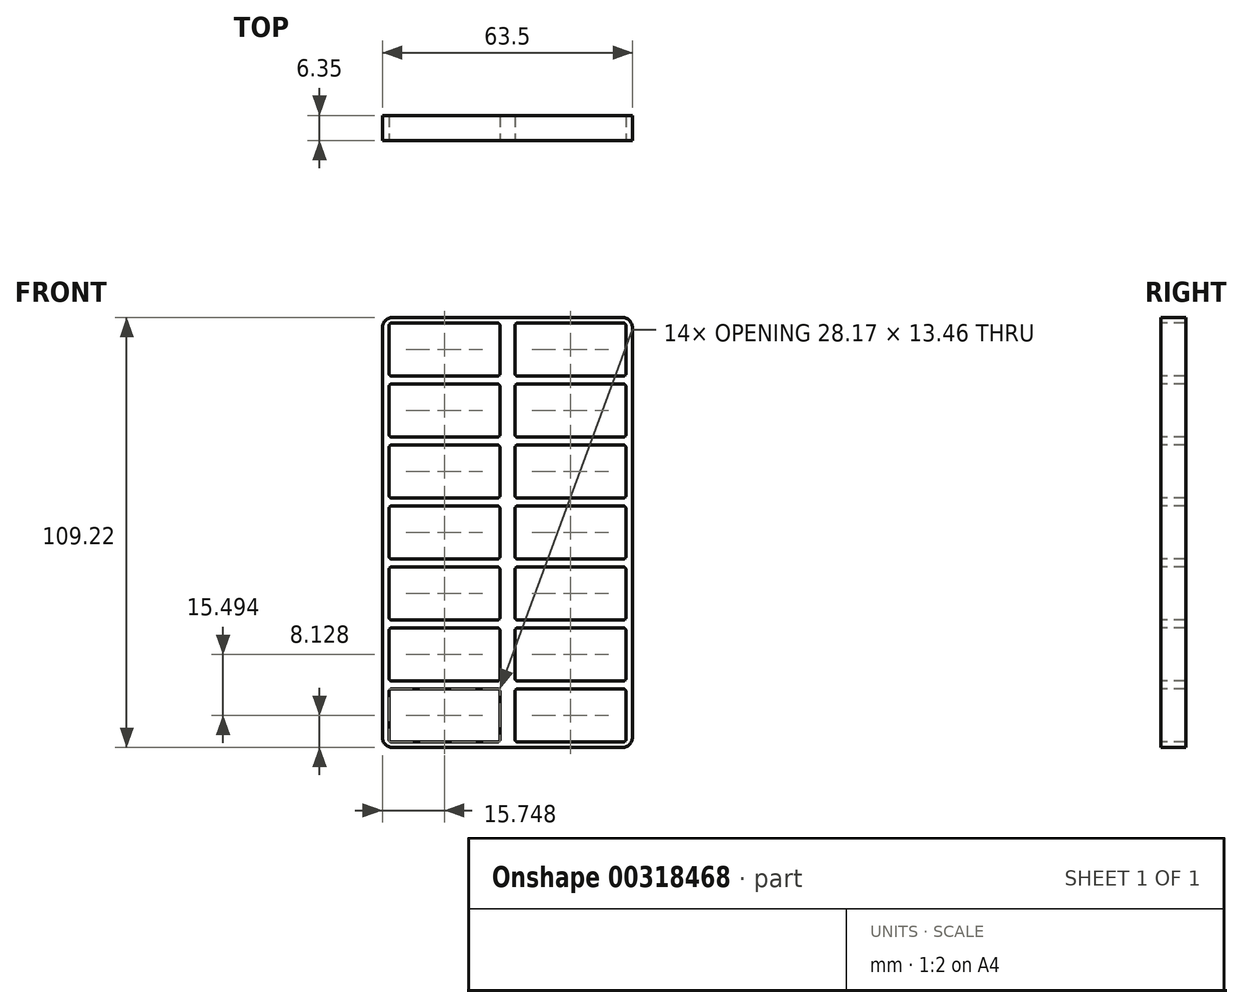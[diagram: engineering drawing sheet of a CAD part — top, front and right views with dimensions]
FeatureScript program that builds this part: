
annotation { "Feature Type Name" : "Feature", "Feature Type Description" : "" }
export const myFeature = defineFeature(function(context is Context, id is Id, definition is map)
    precondition{}
    {
        {
            var Q0;
            Q0=qCreatedBy(makeId("Front.planeOp"),FACE);
            var sketch = newSketch(context, id + "F0", { "sketchPlane" : qUnion([Q0])});
            skLineSegment(sketch, "E0.bottom", {"start": v(-29.2, -54.6) * mm, "end": v(29.21, -54.6) * mm});
            skLineSegment(sketch, "E0.top", {"start": v(-29.21, 54.61) * mm, "end": v(29.2, 54.61) * mm});
            skLineSegment(sketch, "E0.left", {"start": v(-31.75, -52.07) * mm, "end": v(-31.75, 52.07) * mm});
            skLineSegment(sketch, "E0.right", {"start": v(31.75, -52.07) * mm, "end": v(31.75, 52.07) * mm});
            skPoint(sketch, "E0.middle", {"position": v(0, 0) * mm});
            skPoint(sketch, "E1.visualSharp", {"position": v(-31.75, 54.61) * mm});
            skArc(sketch, "E1.filletArc", {"start": v(-29.21, 54.61) * mm, "mid": v(-31, 53.87) * mm, "end": v(-31.75, 52.07) * mm});
            skPoint(sketch, "E2.visualSharp", {"position": v(31.75, 54.61) * mm});
            skArc(sketch, "E2.filletArc", {"start": v(31.75, 52.07) * mm, "mid": v(31, 53.87) * mm, "end": v(29.2, 54.61) * mm});
            skPoint(sketch, "E3.visualSharp", {"position": v(31.75, -54.6) * mm});
            skArc(sketch, "E3.filletArc", {"start": v(29.21, -54.6) * mm, "mid": v(31, -53.87) * mm, "end": v(31.75, -52.07) * mm});
            skPoint(sketch, "E4.visualSharp", {"position": v(-31.75, -54.6) * mm});
            skArc(sketch, "E4.filletArc", {"start": v(-31.75, -52.07) * mm, "mid": v(-31, -53.87) * mm, "end": v(-29.2, -54.6) * mm});
            skSolve(sketch);
        }
        {
            var Q0;
            Q0 = qSketchRegion(id + "F0", true);
            extrude(context, id + "F1", {"entities" : qUnion([Q0]), "depth" : 6.35 * mm, "offsetDistance" : 25.4 * mm});
        }
        {
            var Q0;
            Q0=makeQuery(id+"F1.opExtrude","CAP_FACE",FACE,{"disambiguationData":[OSD([sQuery(id+"F0.wireOp",EDGE,"E0.bottom"),sQuery(id+"F0.wireOp",EDGE,"E0.top"),sQuery(id+"F0.wireOp",EDGE,"E0.left"),sQuery(id+"F0.wireOp",EDGE,"E0.right"),sQuery(id+"F0.wireOp",EDGE,"E1.filletArc"),sQuery(id+"F0.wireOp",EDGE,"E2.filletArc"),sQuery(id+"F0.wireOp",EDGE,"E3.filletArc"),sQuery(id+"F0.wireOp",EDGE,"E4.filletArc")])],"isStart":false});
            var sketch = newSketch(context, id + "F2", { "sketchPlane" : qUnion([Q0])});
            skLineSegment(sketch, "E5.bottom", {"start": v(-2.55, 39.75) * mm, "end": v(-29.45, 39.75) * mm});
            skLineSegment(sketch, "E5.top", {"start": v(-2.55, 53.21) * mm, "end": v(-29.45, 53.21) * mm});
            skLineSegment(sketch, "E5.left", {"start": v(-1.92, 40.39) * mm, "end": v(-1.92, 52.58) * mm});
            skLineSegment(sketch, "E5.right", {"start": v(-30.09, 40.39) * mm, "end": v(-30.09, 52.58) * mm});
            skPoint(sketch, "E5.middle", {"position": v(-16, 46.48) * mm});
            skPoint(sketch, "E6.visualSharp", {"position": v(-30.09, 53.21) * mm});
            skArc(sketch, "E6.filletArc", {"start": v(-29.45, 53.21) * mm, "mid": v(-29.9, 53.03) * mm, "end": v(-30.09, 52.58) * mm});
            skPoint(sketch, "E7.visualSharp", {"position": v(-1.92, 53.21) * mm});
            skArc(sketch, "E7.filletArc", {"start": v(-1.92, 52.58) * mm, "mid": v(-2.1, 53.03) * mm, "end": v(-2.55, 53.21) * mm});
            skPoint(sketch, "E8.visualSharp", {"position": v(-1.92, 39.75) * mm});
            skArc(sketch, "E8.filletArc", {"start": v(-2.55, 39.75) * mm, "mid": v(-2.1, 39.94) * mm, "end": v(-1.92, 40.39) * mm});
            skPoint(sketch, "E9.visualSharp", {"position": v(-30.09, 39.75) * mm});
            skArc(sketch, "E9.filletArc", {"start": v(-30.09, 40.39) * mm, "mid": v(-29.9, 39.94) * mm, "end": v(-29.45, 39.75) * mm});
            skLineSegment(sketch, "E10.0.1.0", {"start": v(-30.09, 24.9) * mm, "end": v(-30.09, 37.08) * mm});
            skLineSegment(sketch, "E10.0.1.1", {"start": v(-2.55, 24.26) * mm, "end": v(-29.45, 24.26) * mm});
            skPoint(sketch, "E10.0.1.2", {"position": v(-16, 30.99) * mm});
            skLineSegment(sketch, "E10.0.1.3", {"start": v(-1.92, 24.9) * mm, "end": v(-1.92, 37.08) * mm});
            skLineSegment(sketch, "E10.0.1.4", {"start": v(-2.55, 37.72) * mm, "end": v(-29.45, 37.72) * mm});
            skPoint(sketch, "E10.0.1.5", {"position": v(-30.09, 37.72) * mm});
            skPoint(sketch, "E10.0.1.6", {"position": v(-1.92, 37.72) * mm});
            skPoint(sketch, "E10.0.1.7", {"position": v(-1.92, 24.26) * mm});
            skPoint(sketch, "E10.0.1.8", {"position": v(-30.09, 24.26) * mm});
            skArc(sketch, "E10.0.1.9", {"start": v(-1.92, 37.08) * mm, "mid": v(-2.1, 37.53) * mm, "end": v(-2.55, 37.72) * mm});
            skArc(sketch, "E10.0.1.10", {"start": v(-2.55, 24.26) * mm, "mid": v(-2.1, 24.44) * mm, "end": v(-1.92, 24.9) * mm});
            skArc(sketch, "E10.0.1.11", {"start": v(-29.45, 37.72) * mm, "mid": v(-29.9, 37.53) * mm, "end": v(-30.09, 37.08) * mm});
            skArc(sketch, "E10.0.1.12", {"start": v(-30.09, 24.9) * mm, "mid": v(-29.9, 24.44) * mm, "end": v(-29.45, 24.26) * mm});
            skLineSegment(sketch, "E10.0.2.0", {"start": v(-30.09, 9.4) * mm, "end": v(-30.09, 21.59) * mm});
            skLineSegment(sketch, "E10.0.2.1", {"start": v(-2.55, 8.76) * mm, "end": v(-29.45, 8.76) * mm});
            skPoint(sketch, "E10.0.2.2", {"position": v(-16, 15.5) * mm});
            skLineSegment(sketch, "E10.0.2.3", {"start": v(-1.92, 9.4) * mm, "end": v(-1.92, 21.59) * mm});
            skLineSegment(sketch, "E10.0.2.4", {"start": v(-2.55, 22.23) * mm, "end": v(-29.45, 22.23) * mm});
            skPoint(sketch, "E10.0.2.5", {"position": v(-30.09, 22.23) * mm});
            skPoint(sketch, "E10.0.2.6", {"position": v(-1.92, 22.23) * mm});
            skPoint(sketch, "E10.0.2.7", {"position": v(-1.92, 8.76) * mm});
            skPoint(sketch, "E10.0.2.8", {"position": v(-30.09, 8.76) * mm});
            skArc(sketch, "E10.0.2.9", {"start": v(-1.92, 21.59) * mm, "mid": v(-2.1, 22.04) * mm, "end": v(-2.55, 22.22) * mm});
            skArc(sketch, "E10.0.2.10", {"start": v(-2.55, 8.76) * mm, "mid": v(-2.1, 8.95) * mm, "end": v(-1.92, 9.4) * mm});
            skArc(sketch, "E10.0.2.11", {"start": v(-29.45, 22.22) * mm, "mid": v(-29.9, 22.04) * mm, "end": v(-30.09, 21.59) * mm});
            skArc(sketch, "E10.0.2.12", {"start": v(-30.09, 9.4) * mm, "mid": v(-29.9, 8.95) * mm, "end": v(-29.45, 8.76) * mm});
            skLineSegment(sketch, "E10.0.3.0", {"start": v(-30.09, -6.1) * mm, "end": v(-30.09, 6.1) * mm});
            skLineSegment(sketch, "E10.0.3.1", {"start": v(-2.55, -6.73) * mm, "end": v(-29.45, -6.73) * mm});
            skPoint(sketch, "E10.0.3.2", {"position": v(-16, 0) * mm});
            skLineSegment(sketch, "E10.0.3.3", {"start": v(-1.92, -6.1) * mm, "end": v(-1.92, 6.1) * mm});
            skLineSegment(sketch, "E10.0.3.4", {"start": v(-2.55, 6.73) * mm, "end": v(-29.45, 6.73) * mm});
            skPoint(sketch, "E10.0.3.5", {"position": v(-30.09, 6.73) * mm});
            skPoint(sketch, "E10.0.3.6", {"position": v(-1.92, 6.73) * mm});
            skPoint(sketch, "E10.0.3.7", {"position": v(-1.92, -6.73) * mm});
            skPoint(sketch, "E10.0.3.8", {"position": v(-30.09, -6.73) * mm});
            skArc(sketch, "E10.0.3.9", {"start": v(-1.92, 6.1) * mm, "mid": v(-2.1, 6.55) * mm, "end": v(-2.55, 6.73) * mm});
            skArc(sketch, "E10.0.3.10", {"start": v(-2.55, -6.73) * mm, "mid": v(-2.1, -6.55) * mm, "end": v(-1.92, -6.1) * mm});
            skArc(sketch, "E10.0.3.11", {"start": v(-29.45, 6.73) * mm, "mid": v(-29.9, 6.55) * mm, "end": v(-30.09, 6.1) * mm});
            skArc(sketch, "E10.0.3.12", {"start": v(-30.09, -6.1) * mm, "mid": v(-29.9, -6.55) * mm, "end": v(-29.45, -6.73) * mm});
            skLineSegment(sketch, "E10.0.4.0", {"start": v(-30.09, -21.59) * mm, "end": v(-30.09, -9.4) * mm});
            skLineSegment(sketch, "E10.0.4.1", {"start": v(-2.55, -22.22) * mm, "end": v(-29.45, -22.22) * mm});
            skPoint(sketch, "E10.0.4.2", {"position": v(-16, -15.5) * mm});
            skLineSegment(sketch, "E10.0.4.3", {"start": v(-1.92, -21.59) * mm, "end": v(-1.92, -9.4) * mm});
            skLineSegment(sketch, "E10.0.4.4", {"start": v(-2.55, -8.76) * mm, "end": v(-29.45, -8.76) * mm});
            skPoint(sketch, "E10.0.4.5", {"position": v(-30.09, -8.76) * mm});
            skPoint(sketch, "E10.0.4.6", {"position": v(-1.92, -8.76) * mm});
            skPoint(sketch, "E10.0.4.7", {"position": v(-1.92, -22.22) * mm});
            skPoint(sketch, "E10.0.4.8", {"position": v(-30.09, -22.22) * mm});
            skArc(sketch, "E10.0.4.9", {"start": v(-1.92, -9.4) * mm, "mid": v(-2.1, -8.95) * mm, "end": v(-2.55, -8.76) * mm});
            skArc(sketch, "E10.0.4.10", {"start": v(-2.55, -22.22) * mm, "mid": v(-2.1, -22.04) * mm, "end": v(-1.92, -21.59) * mm});
            skArc(sketch, "E10.0.4.11", {"start": v(-29.45, -8.76) * mm, "mid": v(-29.9, -8.95) * mm, "end": v(-30.09, -9.4) * mm});
            skArc(sketch, "E10.0.4.12", {"start": v(-30.09, -21.59) * mm, "mid": v(-29.9, -22.04) * mm, "end": v(-29.45, -22.22) * mm});
            skLineSegment(sketch, "E10.0.5.0", {"start": v(-30.09, -37.08) * mm, "end": v(-30.09, -24.9) * mm});
            skLineSegment(sketch, "E10.0.5.1", {"start": v(-2.55, -37.72) * mm, "end": v(-29.45, -37.72) * mm});
            skPoint(sketch, "E10.0.5.2", {"position": v(-16, -30.99) * mm});
            skLineSegment(sketch, "E10.0.5.3", {"start": v(-1.92, -37.08) * mm, "end": v(-1.92, -24.9) * mm});
            skLineSegment(sketch, "E10.0.5.4", {"start": v(-2.55, -24.26) * mm, "end": v(-29.45, -24.26) * mm});
            skPoint(sketch, "E10.0.5.5", {"position": v(-30.09, -24.26) * mm});
            skPoint(sketch, "E10.0.5.6", {"position": v(-1.92, -24.26) * mm});
            skPoint(sketch, "E10.0.5.7", {"position": v(-1.92, -37.72) * mm});
            skPoint(sketch, "E10.0.5.8", {"position": v(-30.09, -37.72) * mm});
            skArc(sketch, "E10.0.5.9", {"start": v(-1.92, -24.9) * mm, "mid": v(-2.1, -24.44) * mm, "end": v(-2.55, -24.26) * mm});
            skArc(sketch, "E10.0.5.10", {"start": v(-2.55, -37.72) * mm, "mid": v(-2.1, -37.53) * mm, "end": v(-1.92, -37.08) * mm});
            skArc(sketch, "E10.0.5.11", {"start": v(-29.45, -24.26) * mm, "mid": v(-29.9, -24.44) * mm, "end": v(-30.09, -24.9) * mm});
            skArc(sketch, "E10.0.5.12", {"start": v(-30.09, -37.08) * mm, "mid": v(-29.9, -37.53) * mm, "end": v(-29.45, -37.72) * mm});
            skLineSegment(sketch, "E10.0.6.0", {"start": v(-30.09, -52.58) * mm, "end": v(-30.09, -40.39) * mm});
            skLineSegment(sketch, "E10.0.6.1", {"start": v(-2.55, -53.21) * mm, "end": v(-29.45, -53.21) * mm});
            skPoint(sketch, "E10.0.6.2", {"position": v(-16, -46.48) * mm});
            skLineSegment(sketch, "E10.0.6.3", {"start": v(-1.92, -52.58) * mm, "end": v(-1.92, -40.39) * mm});
            skLineSegment(sketch, "E10.0.6.4", {"start": v(-2.55, -39.75) * mm, "end": v(-29.45, -39.75) * mm});
            skPoint(sketch, "E10.0.6.5", {"position": v(-30.09, -39.75) * mm});
            skPoint(sketch, "E10.0.6.6", {"position": v(-1.92, -39.75) * mm});
            skPoint(sketch, "E10.0.6.7", {"position": v(-1.92, -53.21) * mm});
            skPoint(sketch, "E10.0.6.8", {"position": v(-30.09, -53.21) * mm});
            skArc(sketch, "E10.0.6.9", {"start": v(-1.92, -40.39) * mm, "mid": v(-2.1, -39.94) * mm, "end": v(-2.55, -39.75) * mm});
            skArc(sketch, "E10.0.6.10", {"start": v(-2.55, -53.21) * mm, "mid": v(-2.1, -53.03) * mm, "end": v(-1.92, -52.58) * mm});
            skArc(sketch, "E10.0.6.11", {"start": v(-29.45, -39.75) * mm, "mid": v(-29.9, -39.94) * mm, "end": v(-30.09, -40.39) * mm});
            skArc(sketch, "E10.0.6.12", {"start": v(-30.09, -52.58) * mm, "mid": v(-29.9, -53.03) * mm, "end": v(-29.45, -53.21) * mm});
            skLineSegment(sketch, "E10.1.0.0", {"start": v(1.92, 40.39) * mm, "end": v(1.92, 52.58) * mm});
            skLineSegment(sketch, "E10.1.0.1", {"start": v(29.45, 39.75) * mm, "end": v(2.55, 39.75) * mm});
            skPoint(sketch, "E10.1.0.2", {"position": v(16, 46.48) * mm});
            skLineSegment(sketch, "E10.1.0.3", {"start": v(30.09, 40.39) * mm, "end": v(30.09, 52.58) * mm});
            skLineSegment(sketch, "E10.1.0.4", {"start": v(29.45, 53.21) * mm, "end": v(2.55, 53.21) * mm});
            skPoint(sketch, "E10.1.0.5", {"position": v(1.92, 53.21) * mm});
            skPoint(sketch, "E10.1.0.6", {"position": v(30.09, 53.21) * mm});
            skPoint(sketch, "E10.1.0.7", {"position": v(30.09, 39.75) * mm});
            skPoint(sketch, "E10.1.0.8", {"position": v(1.92, 39.75) * mm});
            skArc(sketch, "E10.1.0.9", {"start": v(30.09, 52.58) * mm, "mid": v(29.9, 53.03) * mm, "end": v(29.45, 53.21) * mm});
            skArc(sketch, "E10.1.0.10", {"start": v(29.45, 39.75) * mm, "mid": v(29.9, 39.94) * mm, "end": v(30.09, 40.39) * mm});
            skArc(sketch, "E10.1.0.11", {"start": v(2.55, 53.21) * mm, "mid": v(2.1, 53.03) * mm, "end": v(1.92, 52.58) * mm});
            skArc(sketch, "E10.1.0.12", {"start": v(1.92, 40.39) * mm, "mid": v(2.1, 39.94) * mm, "end": v(2.55, 39.75) * mm});
            skLineSegment(sketch, "E10.1.1.0", {"start": v(1.92, 24.9) * mm, "end": v(1.92, 37.08) * mm});
            skLineSegment(sketch, "E10.1.1.1", {"start": v(29.45, 24.26) * mm, "end": v(2.55, 24.26) * mm});
            skPoint(sketch, "E10.1.1.2", {"position": v(16, 30.99) * mm});
            skLineSegment(sketch, "E10.1.1.3", {"start": v(30.09, 24.9) * mm, "end": v(30.09, 37.08) * mm});
            skLineSegment(sketch, "E10.1.1.4", {"start": v(29.45, 37.72) * mm, "end": v(2.55, 37.72) * mm});
            skPoint(sketch, "E10.1.1.5", {"position": v(1.92, 37.72) * mm});
            skPoint(sketch, "E10.1.1.6", {"position": v(30.09, 37.72) * mm});
            skPoint(sketch, "E10.1.1.7", {"position": v(30.09, 24.26) * mm});
            skPoint(sketch, "E10.1.1.8", {"position": v(1.92, 24.26) * mm});
            skArc(sketch, "E10.1.1.9", {"start": v(30.09, 37.08) * mm, "mid": v(29.9, 37.53) * mm, "end": v(29.45, 37.72) * mm});
            skArc(sketch, "E10.1.1.10", {"start": v(29.45, 24.26) * mm, "mid": v(29.9, 24.44) * mm, "end": v(30.09, 24.9) * mm});
            skArc(sketch, "E10.1.1.11", {"start": v(2.55, 37.72) * mm, "mid": v(2.1, 37.53) * mm, "end": v(1.92, 37.08) * mm});
            skArc(sketch, "E10.1.1.12", {"start": v(1.92, 24.9) * mm, "mid": v(2.1, 24.44) * mm, "end": v(2.55, 24.26) * mm});
            skLineSegment(sketch, "E10.1.2.0", {"start": v(1.92, 9.4) * mm, "end": v(1.92, 21.6) * mm});
            skLineSegment(sketch, "E10.1.2.1", {"start": v(29.45, 8.76) * mm, "end": v(2.55, 8.76) * mm});
            skPoint(sketch, "E10.1.2.2", {"position": v(16, 15.5) * mm});
            skLineSegment(sketch, "E10.1.2.3", {"start": v(30.09, 9.4) * mm, "end": v(30.09, 21.6) * mm});
            skLineSegment(sketch, "E10.1.2.4", {"start": v(29.45, 22.23) * mm, "end": v(2.55, 22.23) * mm});
            skPoint(sketch, "E10.1.2.5", {"position": v(1.92, 22.23) * mm});
            skPoint(sketch, "E10.1.2.6", {"position": v(30.09, 22.23) * mm});
            skPoint(sketch, "E10.1.2.7", {"position": v(30.09, 8.76) * mm});
            skPoint(sketch, "E10.1.2.8", {"position": v(1.92, 8.76) * mm});
            skArc(sketch, "E10.1.2.9", {"start": v(30.09, 21.6) * mm, "mid": v(29.9, 22.04) * mm, "end": v(29.45, 22.22) * mm});
            skArc(sketch, "E10.1.2.10", {"start": v(29.45, 8.76) * mm, "mid": v(29.9, 8.95) * mm, "end": v(30.09, 9.4) * mm});
            skArc(sketch, "E10.1.2.11", {"start": v(2.55, 22.22) * mm, "mid": v(2.1, 22.04) * mm, "end": v(1.92, 21.6) * mm});
            skArc(sketch, "E10.1.2.12", {"start": v(1.92, 9.4) * mm, "mid": v(2.1, 8.95) * mm, "end": v(2.55, 8.76) * mm});
            skLineSegment(sketch, "E10.1.3.0", {"start": v(1.92, -6.1) * mm, "end": v(1.92, 6.1) * mm});
            skLineSegment(sketch, "E10.1.3.1", {"start": v(29.45, -6.73) * mm, "end": v(2.55, -6.73) * mm});
            skPoint(sketch, "E10.1.3.2", {"position": v(16, 0) * mm});
            skLineSegment(sketch, "E10.1.3.3", {"start": v(30.09, -6.1) * mm, "end": v(30.09, 6.1) * mm});
            skLineSegment(sketch, "E10.1.3.4", {"start": v(29.45, 6.73) * mm, "end": v(2.55, 6.73) * mm});
            skPoint(sketch, "E10.1.3.5", {"position": v(1.92, 6.73) * mm});
            skPoint(sketch, "E10.1.3.6", {"position": v(30.09, 6.73) * mm});
            skPoint(sketch, "E10.1.3.7", {"position": v(30.09, -6.73) * mm});
            skPoint(sketch, "E10.1.3.8", {"position": v(1.92, -6.73) * mm});
            skArc(sketch, "E10.1.3.9", {"start": v(30.09, 6.1) * mm, "mid": v(29.9, 6.55) * mm, "end": v(29.45, 6.73) * mm});
            skArc(sketch, "E10.1.3.10", {"start": v(29.45, -6.73) * mm, "mid": v(29.9, -6.55) * mm, "end": v(30.09, -6.1) * mm});
            skArc(sketch, "E10.1.3.11", {"start": v(2.55, 6.73) * mm, "mid": v(2.1, 6.55) * mm, "end": v(1.92, 6.1) * mm});
            skArc(sketch, "E10.1.3.12", {"start": v(1.92, -6.1) * mm, "mid": v(2.1, -6.55) * mm, "end": v(2.55, -6.73) * mm});
            skLineSegment(sketch, "E10.1.4.0", {"start": v(1.92, -21.59) * mm, "end": v(1.92, -9.4) * mm});
            skLineSegment(sketch, "E10.1.4.1", {"start": v(29.45, -22.22) * mm, "end": v(2.55, -22.22) * mm});
            skPoint(sketch, "E10.1.4.2", {"position": v(16, -15.5) * mm});
            skLineSegment(sketch, "E10.1.4.3", {"start": v(30.09, -21.59) * mm, "end": v(30.09, -9.4) * mm});
            skLineSegment(sketch, "E10.1.4.4", {"start": v(29.45, -8.76) * mm, "end": v(2.55, -8.76) * mm});
            skPoint(sketch, "E10.1.4.5", {"position": v(1.92, -8.76) * mm});
            skPoint(sketch, "E10.1.4.6", {"position": v(30.09, -8.76) * mm});
            skPoint(sketch, "E10.1.4.7", {"position": v(30.09, -22.22) * mm});
            skPoint(sketch, "E10.1.4.8", {"position": v(1.92, -22.22) * mm});
            skArc(sketch, "E10.1.4.9", {"start": v(30.09, -9.4) * mm, "mid": v(29.9, -8.95) * mm, "end": v(29.45, -8.76) * mm});
            skArc(sketch, "E10.1.4.10", {"start": v(29.45, -22.22) * mm, "mid": v(29.9, -22.04) * mm, "end": v(30.09, -21.59) * mm});
            skArc(sketch, "E10.1.4.11", {"start": v(2.55, -8.76) * mm, "mid": v(2.1, -8.95) * mm, "end": v(1.92, -9.4) * mm});
            skArc(sketch, "E10.1.4.12", {"start": v(1.92, -21.59) * mm, "mid": v(2.1, -22.04) * mm, "end": v(2.55, -22.22) * mm});
            skLineSegment(sketch, "E10.1.5.0", {"start": v(1.92, -37.08) * mm, "end": v(1.92, -24.9) * mm});
            skLineSegment(sketch, "E10.1.5.1", {"start": v(29.45, -37.72) * mm, "end": v(2.55, -37.72) * mm});
            skPoint(sketch, "E10.1.5.2", {"position": v(16, -30.99) * mm});
            skLineSegment(sketch, "E10.1.5.3", {"start": v(30.09, -37.08) * mm, "end": v(30.09, -24.9) * mm});
            skLineSegment(sketch, "E10.1.5.4", {"start": v(29.45, -24.26) * mm, "end": v(2.55, -24.26) * mm});
            skPoint(sketch, "E10.1.5.5", {"position": v(1.92, -24.26) * mm});
            skPoint(sketch, "E10.1.5.6", {"position": v(30.09, -24.26) * mm});
            skPoint(sketch, "E10.1.5.7", {"position": v(30.09, -37.72) * mm});
            skPoint(sketch, "E10.1.5.8", {"position": v(1.92, -37.72) * mm});
            skArc(sketch, "E10.1.5.9", {"start": v(30.09, -24.9) * mm, "mid": v(29.9, -24.44) * mm, "end": v(29.45, -24.26) * mm});
            skArc(sketch, "E10.1.5.10", {"start": v(29.45, -37.72) * mm, "mid": v(29.9, -37.53) * mm, "end": v(30.09, -37.08) * mm});
            skArc(sketch, "E10.1.5.11", {"start": v(2.55, -24.26) * mm, "mid": v(2.1, -24.44) * mm, "end": v(1.92, -24.9) * mm});
            skArc(sketch, "E10.1.5.12", {"start": v(1.92, -37.08) * mm, "mid": v(2.1, -37.53) * mm, "end": v(2.55, -37.72) * mm});
            skLineSegment(sketch, "E10.1.6.0", {"start": v(1.92, -52.58) * mm, "end": v(1.92, -40.39) * mm});
            skLineSegment(sketch, "E10.1.6.1", {"start": v(29.45, -53.21) * mm, "end": v(2.55, -53.21) * mm});
            skPoint(sketch, "E10.1.6.2", {"position": v(16, -46.48) * mm});
            skLineSegment(sketch, "E10.1.6.3", {"start": v(30.09, -52.58) * mm, "end": v(30.09, -40.39) * mm});
            skLineSegment(sketch, "E10.1.6.4", {"start": v(29.45, -39.75) * mm, "end": v(2.55, -39.75) * mm});
            skPoint(sketch, "E10.1.6.5", {"position": v(1.92, -39.75) * mm});
            skPoint(sketch, "E10.1.6.6", {"position": v(30.09, -39.75) * mm});
            skPoint(sketch, "E10.1.6.7", {"position": v(30.09, -53.21) * mm});
            skPoint(sketch, "E10.1.6.8", {"position": v(1.92, -53.21) * mm});
            skArc(sketch, "E10.1.6.9", {"start": v(30.09, -40.39) * mm, "mid": v(29.9, -39.94) * mm, "end": v(29.45, -39.75) * mm});
            skArc(sketch, "E10.1.6.10", {"start": v(29.45, -53.21) * mm, "mid": v(29.9, -53.03) * mm, "end": v(30.09, -52.58) * mm});
            skArc(sketch, "E10.1.6.11", {"start": v(2.55, -39.75) * mm, "mid": v(2.1, -39.94) * mm, "end": v(1.92, -40.39) * mm});
            skArc(sketch, "E10.1.6.12", {"start": v(1.92, -52.58) * mm, "mid": v(2.1, -53.03) * mm, "end": v(2.55, -53.21) * mm});
            skLineSegment(sketch, "E10.direction1", {"start": v(-30.09, 39.75) * mm, "end": v(1.92, 39.75) * mm, "construction": true});
            skLineSegment(sketch, "E10.direction2", {"start": v(-30.09, 39.75) * mm, "end": v(-30.09, 24.26) * mm, "construction": true});
            skSolve(sketch);
        }
        {
            var Q0;
            Q0 = qSketchRegion(id + "F2", true);
            extrude(context, id + "F3", {"entities" : qUnion([Q0]), "operationType" : NewBodyOperationType.REMOVE, "endBound" : BoundingType.THROUGH_ALL, "oppositeDirection" : true, "depth" : 25.4 * mm, "offsetDistance" : 25.4 * mm});
        }
    });
